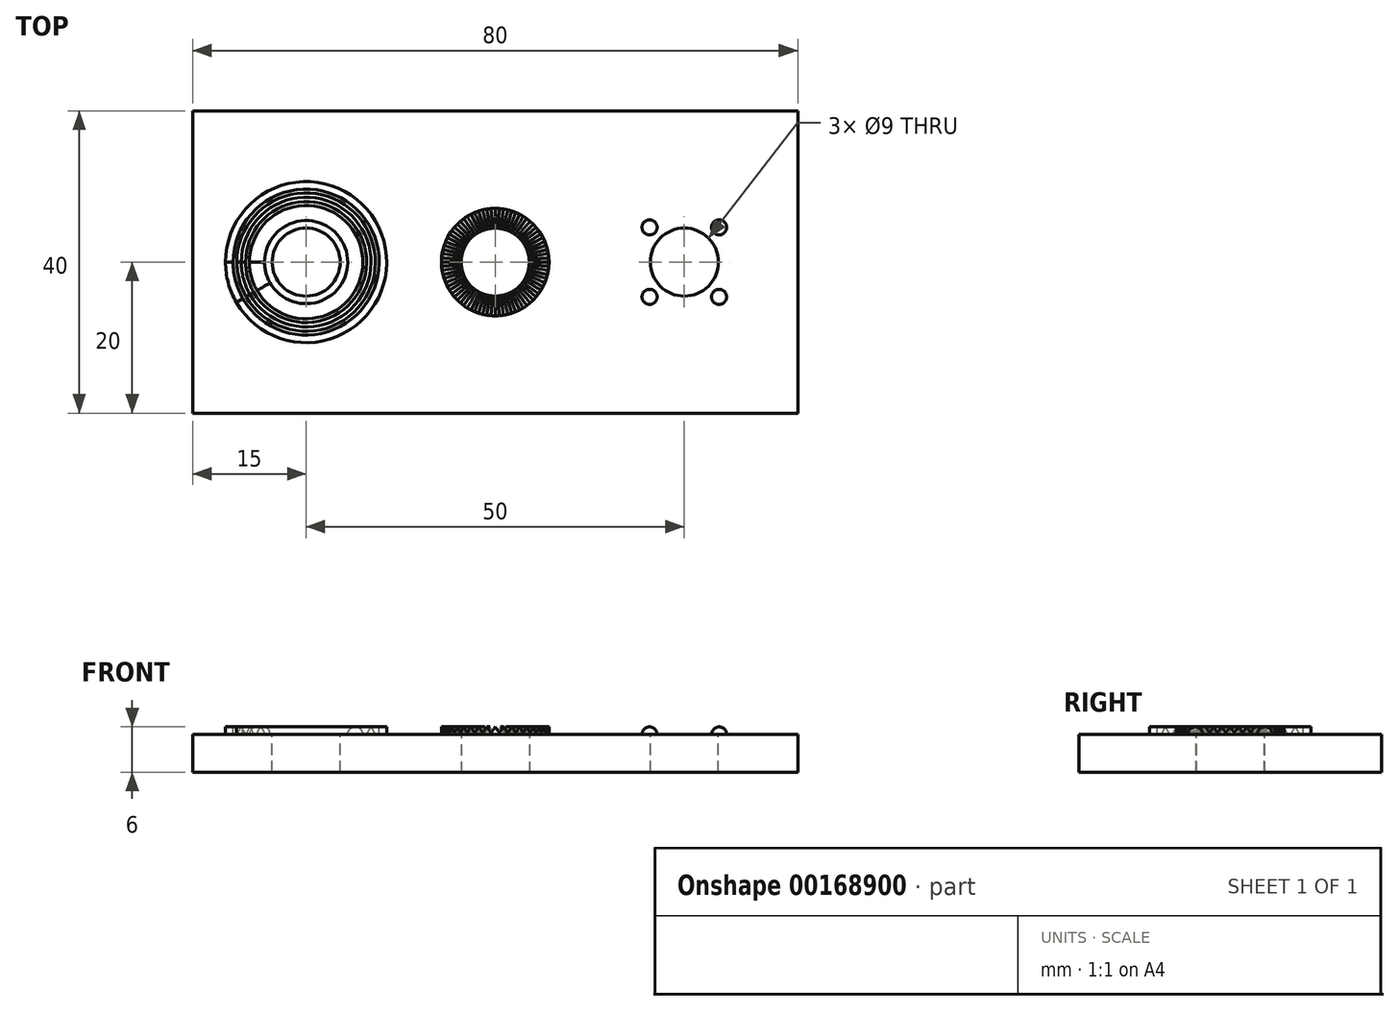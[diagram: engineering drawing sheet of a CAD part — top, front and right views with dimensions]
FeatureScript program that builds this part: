
annotation { "Feature Type Name" : "Feature", "Feature Type Description" : "" }
export const myFeature = defineFeature(function(context is Context, id is Id, definition is map)
    precondition{}
    {
        {
            var Q0;
            Q0=qCreatedBy(makeId("Top.planeOp"),FACE);
            var sketch = newSketch(context, id + "F0", { "sketchPlane" : qUnion([Q0])});
            skLineSegment(sketch, "E0.bottom", {"start": v(-40, -20) * mm, "end": v(40, -20) * mm});
            skLineSegment(sketch, "E0.top", {"start": v(-40, 20) * mm, "end": v(40, 20) * mm});
            skLineSegment(sketch, "E0.left", {"start": v(-40, -20) * mm, "end": v(-40, 20) * mm});
            skLineSegment(sketch, "E0.right", {"start": v(40, -20) * mm, "end": v(40, 20) * mm});
            skPoint(sketch, "E0.middle", {"position": v(0, 0) * mm});
            skSolve(sketch);
        }
        {
            var Q0;
            Q0=makeQuery(id+"F0.imprint","IMPRINT",FACE,{"disambiguationData":[TD([[makeQuery(id+"F0.imprint","IMPRINT",EDGE,{"derivedFrom":sQuery(id+"F0.wireOp",EDGE,"E0.bottom")}),1.0]])]});
            extrude(context, id + "F1", {"entities" : qUnion([Q0]), "depth" : 5 * mm});
        }
        {
            var Q0;
            Q0=makeQuery(id+"F1.opExtrude","CAP_FACE",FACE,{"disambiguationData":[OSD([sQuery(id+"F0.wireOp",EDGE,"E0.bottom"),sQuery(id+"F0.wireOp",EDGE,"E0.top"),sQuery(id+"F0.wireOp",EDGE,"E0.left"),sQuery(id+"F0.wireOp",EDGE,"E0.right")])],"isStart":false});
            var sketch = newSketch(context, id + "F2", { "sketchPlane" : qUnion([Q0])});
            skPoint(sketch, "E1", {"position": v(-25, 0) * mm});
            skPoint(sketch, "E2", {"position": v(0, 0) * mm});
            skPoint(sketch, "E3", {"position": v(25, 0) * mm});
            skSolve(sketch);
        }
        {
            var Q0;
            Q0=qCreatedBy(makeId("Front.planeOp"),FACE);
            var sketch = newSketch(context, id + "F3", { "sketchPlane" : qUnion([Q0])});
            skPoint(sketch, "E4.0", {"position": v(0, 5) * mm});
            skLineSegment(sketch, "E5", {"start": v(0, 5) * mm, "end": v(0, 6) * mm});
            skSolve(sketch);
        }
        {
            var Q0;
            Q0=makeQuery(id+"F1.opExtrude","SWEPT_FACE",FACE,{"disambiguationData":[OSD([sQuery(id+"F0.wireOp",EDGE,"E0.bottom")])]});
            cPlane(context, id + "F4", {"entities" : qUnion([Q0]), "cplaneType" : CPlaneType.OFFSET, "offset" : 10 * mm, "oppositeDirection" : true, "width" : 150 * mm, "height" : 150 * mm});
        }
        {
            var Q0;
            Q0=makeQuery(id+"F2.imprint","IMPRINT",FACE,{"disambiguationData":[TD([[makeQuery(id+"F2.imprint","IMPRINT",EDGE,{"derivedFrom":makeQuery(id+"F1.opExtrude","CAP_EDGE",EDGE,{"disambiguationData":[OSD([sQuery(id+"F0.wireOp",EDGE,"E0.bottom")])],"isStart":false})}),1.0]])]});
            var sketch = newSketch(context, id + "F5", { "sketchPlane" : qUnion([Q0])});
            skLineSegment(sketch, "E6", {"start": v(0, 0) * mm, "end": v(-1.57, -19.94) * mm, "construction": true});
            skLineSegment(sketch, "E7", {"start": v(0, 0) * mm, "end": v(1.57, -19.94) * mm, "construction": true});
            skLineSegment(sketch, "E8", {"start": v(0, 0) * mm, "end": v(0, -22) * mm, "construction": true});
            skSolve(sketch);
        }
        {
            var Q0;
            Q0=qCreatedBy(id+"F4.planeOp",FACE);
            var sketch = newSketch(context, id + "F6", { "sketchPlane" : qUnion([Q0])});
            skLineSegment(sketch, "E9", {"start": v(0, 6) * mm, "end": v(-0.79, 5) * mm});
            skLineSegment(sketch, "E10", {"start": v(0.79, 5) * mm, "end": v(0, 6) * mm});
            skLineSegment(sketch, "E11", {"start": v(-0.79, 5) * mm, "end": v(0.79, 5) * mm});
            skSolve(sketch);
        }
        {
            var Q0;
            Q0=makeQuery(id+"F1.opExtrude","SWEPT_FACE",FACE,{"disambiguationData":[OSD([sQuery(id+"F0.wireOp",EDGE,"E0.bottom")])]});
            cPlane(context, id + "F7", {"entities" : qUnion([Q0]), "cplaneType" : CPlaneType.OFFSET, "offset" : 24 * mm, "oppositeDirection" : true, "width" : 150 * mm, "height" : 150 * mm});
        }
        {
            var Q0;
            Q0=qCreatedBy(id+"F7.planeOp",FACE);
            var sketch = newSketch(context, id + "F8", { "sketchPlane" : qUnion([Q0])});
            skLineSegment(sketch, "E12", {"start": v(-0.31, 5) * mm, "end": v(0.31, 5) * mm});
            skLineSegment(sketch, "E13", {"start": v(0, 6) * mm, "end": v(0.31, 5) * mm});
            skLineSegment(sketch, "E14", {"start": v(-0.31, 5) * mm, "end": v(0, 6) * mm});
            skSolve(sketch);
        }
        {
            var Q1;
            Q1 = qSketchRegion(id + "F8", true);
            var Q2;
            Q2 = qSketchRegion(id + "F6", true);
            loft(context, id + "F9", {"sheetProfilesArray" : [{ "sheetProfileEntities" : qUnion([Q1]) }, { "sheetProfileEntities" : qUnion([Q2]) }]});
        }
        {
            var Q0;
            Q0=makeQuery(id+"F9.opLoft","SWEPT_BODY",BODY,{"disambiguationData":[OSD([makeQuery(id+"F6.imprint","IMPRINT",FACE,{"disambiguationData":[TD([[makeQuery(id+"F6.imprint","IMPRINT",EDGE,{"derivedFrom":sQuery(id+"F6.wireOp",EDGE,"E9")}),-1.0]])]}),makeQuery(id+"F8.imprint","IMPRINT",FACE,{"disambiguationData":[TD([[makeQuery(id+"F8.imprint","IMPRINT",EDGE,{"derivedFrom":sQuery(id+"F8.wireOp",EDGE,"E12")}),1.0]])]})])]});
            var Q1;
            Q1=sQuery(id+"F3.wireOp",EDGE,"E5");
            circularPattern(context, id + "F10", {"operationType" : NewBodyOperationType.ADD, "entities" : qUnion([Q0]), "axis" : qUnion([Q1]), "angle" : 360 * degree, "instanceCount" : 40, "equalSpace" : true});
        }
        {
            var Q0;
            Q0=makeQuery(id+"F2.imprint","IMPRINT",FACE,{"disambiguationData":[TD([[makeQuery(id+"F2.imprint","IMPRINT",EDGE,{"derivedFrom":makeQuery(id+"F1.opExtrude","CAP_EDGE",EDGE,{"disambiguationData":[OSD([sQuery(id+"F0.wireOp",EDGE,"E0.bottom")])],"isStart":false})}),1.0]])]});
            var sketch = newSketch(context, id + "F11", { "sketchPlane" : qUnion([Q0])});
            skCircle(sketch, "E15", {"center": v(0, 0) * mm, "radius": 7.1 * mm});
            skCircle(sketch, "E16", {"center": v(0, 0) * mm, "radius": 25 * mm});
            skSolve(sketch);
        }
        {
            var Q0;
            Q0=makeQuery(id+"F11.imprint","IMPRINT",FACE,{"disambiguationData":[TD([[makeQuery(id+"F11.imprint","IMPRINT",EDGE,{"derivedFrom":sQuery(id+"F11.wireOp",EDGE,"E15")}),-1.0]])]});
            extrude(context, id + "F12", {"entities" : qUnion([Q0]), "operationType" : NewBodyOperationType.REMOVE, "depth" : 25 * mm});
        }
        {
            var Q0;
            Q0=makeQuery(id+"F1.opExtrude","CAP_FACE",FACE,{"disambiguationData":[OSD([sQuery(id+"F0.wireOp",EDGE,"E0.bottom"),sQuery(id+"F0.wireOp",EDGE,"E0.top"),sQuery(id+"F0.wireOp",EDGE,"E0.left"),sQuery(id+"F0.wireOp",EDGE,"E0.right")])],"isStart":true});
            var sketch = newSketch(context, id + "F13", { "sketchPlane" : qUnion([Q0])});
            skCircle(sketch, "E17", {"center": v(0, 0) * mm, "radius": 4.5 * mm});
            skSolve(sketch);
        }
        {
            var Q0;
            Q0=makeQuery(id+"F13.imprint","IMPRINT",FACE,{"disambiguationData":[TD([[makeQuery(id+"F13.imprint","IMPRINT",EDGE,{"derivedFrom":sQuery(id+"F13.wireOp",EDGE,"E17")}),1.0]])]});
            extrude(context, id + "F14", {"entities" : qUnion([Q0]), "operationType" : NewBodyOperationType.REMOVE, "endBound" : BoundingType.THROUGH_ALL, "oppositeDirection" : true, "depth" : 25 * mm});
        }
        {
            var Q0;
            Q0=makeQuery(id+"F2.imprint","IMPRINT",FACE,{"disambiguationData":[TD([[makeQuery(id+"F2.imprint","IMPRINT",EDGE,{"derivedFrom":makeQuery(id+"F1.opExtrude","CAP_EDGE",EDGE,{"disambiguationData":[OSD([sQuery(id+"F0.wireOp",EDGE,"E0.bottom")])],"isStart":false})}),1.0]])]});
            var sketch = newSketch(context, id + "F15", { "sketchPlane" : qUnion([Q0])});
            skPoint(sketch, "E18.0", {"position": v(-25, 0) * mm});
            skCircle(sketch, "E19", {"center": v(-25, 0) * mm, "radius": 4.5 * mm});
            skPoint(sketch, "E20.0", {"position": v(25, 0) * mm});
            skCircle(sketch, "E21", {"center": v(25, 0) * mm, "radius": 4.5 * mm});
            skSolve(sketch);
        }
        {
            var Q0;
            Q0 = qSketchRegion(id + "F15", true);
            extrude(context, id + "F16", {"entities" : qUnion([Q0]), "operationType" : NewBodyOperationType.REMOVE, "endBound" : BoundingType.THROUGH_ALL, "oppositeDirection" : true, "depth" : 25 * mm});
        }
        {
            var Q0;
            Q0=makeQuery(id+"F1.opExtrude","SWEPT_FACE",FACE,{"disambiguationData":[OSD([sQuery(id+"F0.wireOp",EDGE,"E0.bottom")])]});
            var Q1;
            Q1=sQuery(id+"F2.wireOp",VERTEX,"E1");
            cPlane(context, id + "F17", {"entities" : qUnion([Q0, Q1]), "cplaneType" : CPlaneType.PLANE_POINT, "offset" : 25 * mm, "width" : 150 * mm, "height" : 150 * mm});
        }
        {
            var Q0;
            Q0=qCreatedBy(id+"F17.planeOp",FACE);
            var sketch = newSketch(context, id + "F18", { "sketchPlane" : qUnion([Q0])});
            skLineSegment(sketch, "E22", {"start": v(-25, 15) * mm, "end": v(-25, 5) * mm, "construction": true});
            skLineSegment(sketch, "E23", {"start": v(-32.5, 5) * mm, "end": v(-30.5, 5) * mm});
            skArc(sketch, "E24", {"start": v(-30.5, 5) * mm, "mid": v(-31.5, 6) * mm, "end": v(-32.5, 5) * mm});
            skLineSegment(sketch, "E25.trimOffspring", {"start": v(-25, 5) * mm, "end": v(40, 5) * mm});
            skPoint(sketch, "E26.orphan", {"position": v(-40, 5) * mm});
            skLineSegment(sketch, "E27", {"start": v(-33, 5) * mm, "end": v(-34.15, 5) * mm});
            skLineSegment(sketch, "E28", {"start": v(-34.15, 5) * mm, "end": v(-33.58, 6) * mm});
            skLineSegment(sketch, "E29", {"start": v(-33.58, 6) * mm, "end": v(-33, 5) * mm});
            skLineSegment(sketch, "E30.bottom", {"start": v(-34.65, 5) * mm, "end": v(-35.65, 5) * mm});
            skLineSegment(sketch, "E30.top", {"start": v(-34.65, 6) * mm, "end": v(-35.65, 6) * mm});
            skLineSegment(sketch, "E30.left", {"start": v(-34.65, 5) * mm, "end": v(-34.65, 6) * mm});
            skLineSegment(sketch, "E30.right", {"start": v(-35.65, 5) * mm, "end": v(-35.65, 6) * mm});
            skSolve(sketch);
        }
        {
            var Q0;
            Q0=makeQuery(id+"F18.imprint","IMPRINT",FACE,{"disambiguationData":[TD([[makeQuery(id+"F18.imprint","IMPRINT",EDGE,{"derivedFrom":sQuery(id+"F18.wireOp",EDGE,"E30.bottom")}),-1.0]])]});
            var Q1;
            Q1=makeQuery(id+"F18.imprint","IMPRINT",FACE,{"disambiguationData":[TD([[makeQuery(id+"F18.imprint","IMPRINT",EDGE,{"derivedFrom":sQuery(id+"F18.wireOp",EDGE,"E27")}),-1.0]])]});
            var Q2;
            Q2=makeQuery(id+"F18.imprint","IMPRINT",FACE,{"disambiguationData":[TD([[makeQuery(id+"F18.imprint","IMPRINT",EDGE,{"derivedFrom":sQuery(id+"F18.wireOp",EDGE,"E24")}),1.0]])]});
            var Q3;
            Q3=sQuery(id+"F18.wireOp",EDGE,"E22");
            revolve(context, id + "F19", {"operationType" : NewBodyOperationType.ADD, "entities" : qUnion([Q0, Q1, Q2]), "axis" : qUnion([Q3]), "revolveType" : RevolveType.ONE_DIRECTION, "angle" : 330 * degree});
        }
        {
            var Q0;
            Q0=makeQuery(id+"F18.imprint","IMPRINT",FACE,{"disambiguationData":[TD([[makeQuery(id+"F18.imprint","IMPRINT",EDGE,{"derivedFrom":sQuery(id+"F18.wireOp",EDGE,"E30.bottom")}),-1.0]])]});
            var Q1;
            Q1=makeQuery(id+"F18.imprint","IMPRINT",FACE,{"disambiguationData":[TD([[makeQuery(id+"F18.imprint","IMPRINT",EDGE,{"derivedFrom":sQuery(id+"F18.wireOp",EDGE,"E27")}),-1.0]])]});
            var Q2;
            Q2=makeQuery(id+"F18.imprint","IMPRINT",FACE,{"disambiguationData":[TD([[makeQuery(id+"F18.imprint","IMPRINT",EDGE,{"derivedFrom":sQuery(id+"F18.wireOp",EDGE,"E24")}),1.0]])]});
            var Q3;
            Q3=sQuery(id+"F18.wireOp",EDGE,"E22");
            revolve(context, id + "F20", {"entities" : qUnion([Q0, Q1, Q2]), "axis" : qUnion([Q3]), "revolveType" : RevolveType.ONE_DIRECTION, "oppositeDirection" : true, "angle" : 30 * degree});
        }
        {
            var Q0;
            Q0=makeQuery(id+"F2.imprint","IMPRINT",FACE,{"disambiguationData":[TD([[makeQuery(id+"F2.imprint","IMPRINT",EDGE,{"derivedFrom":makeQuery(id+"F1.opExtrude","CAP_EDGE",EDGE,{"disambiguationData":[OSD([sQuery(id+"F0.wireOp",EDGE,"E0.bottom")])],"isStart":false})}),1.0]])]});
            var sketch = newSketch(context, id + "F21", { "sketchPlane" : qUnion([Q0])});
            skPoint(sketch, "E31.0", {"position": v(25, 0) * mm});
            skLineSegment(sketch, "E32", {"start": v(25, 0) * mm, "end": v(46.59, 21.59) * mm, "construction": true});
            skLineSegment(sketch, "E33", {"start": v(25, 0) * mm, "end": v(46.96, 0) * mm, "construction": true});
            skSolve(sketch);
        }
        {
            var Q0;
            Q0=sQuery(id+"F21.wireOp",EDGE,"E32");
            cPlane(context, id + "F22", {"entities" : qUnion([Q0]), "cplaneType" : CPlaneType.LINE_ANGLE, "offset" : 25 * mm, "angle" : 90 * degree, "width" : 150 * mm, "height" : 150 * mm});
        }
        {
            var Q0;
            Q0=qCreatedBy(id+"F22.planeOp",FACE);
            var sketch = newSketch(context, id + "F23", { "sketchPlane" : qUnion([Q0])});
            skLineSegment(sketch, "E34", {"start": v(24.18, 5) * mm, "end": v(25.18, 5) * mm});
            skArc(sketch, "E35", {"start": v(25.18, 5) * mm, "mid": v(24.88, 5.7) * mm, "end": v(24.18, 6) * mm});
            skLineSegment(sketch, "E36", {"start": v(24.18, 5) * mm, "end": v(24.18, 6) * mm});
            skLineSegment(sketch, "E37.0", {"start": v(13.18, 5) * mm, "end": v(22.18, 5) * mm, "construction": true});
            skLineSegment(sketch, "E38", {"start": v(17.68, 5) * mm, "end": v(17.68, 11.19) * mm, "construction": true});
            skSolve(sketch);
        }
        {
            var Q0;
            Q0=makeQuery(id+"F23.imprint","IMPRINT",FACE,{"disambiguationData":[TD([[makeQuery(id+"F23.imprint","IMPRINT",EDGE,{"derivedFrom":sQuery(id+"F23.wireOp",EDGE,"E34")}),1.0]])]});
            var Q1;
            Q1=sQuery(id+"F23.wireOp",EDGE,"E36");
            revolve(context, id + "F24", {"entities" : qUnion([Q0]), "axis" : qUnion([Q1]), "revolveType" : RevolveType.FULL});
        }
        {
            var Q0;
            Q0=makeQuery(id+"F24.opRevolve","SWEPT_BODY",BODY,{"disambiguationData":[OSD([sQuery(id+"F23.wireOp",EDGE,"E34"),sQuery(id+"F23.wireOp",EDGE,"E35"),sQuery(id+"F23.wireOp",EDGE,"E36")])]});
            var Q1;
            Q1=sQuery(id+"F23.wireOp",EDGE,"E38");
            circularPattern(context, id + "F25", {"operationType" : NewBodyOperationType.ADD, "entities" : qUnion([Q0]), "axis" : qUnion([Q1]), "angle" : 360 * degree, "instanceCount" : 4, "equalSpace" : true});
        }
    });
